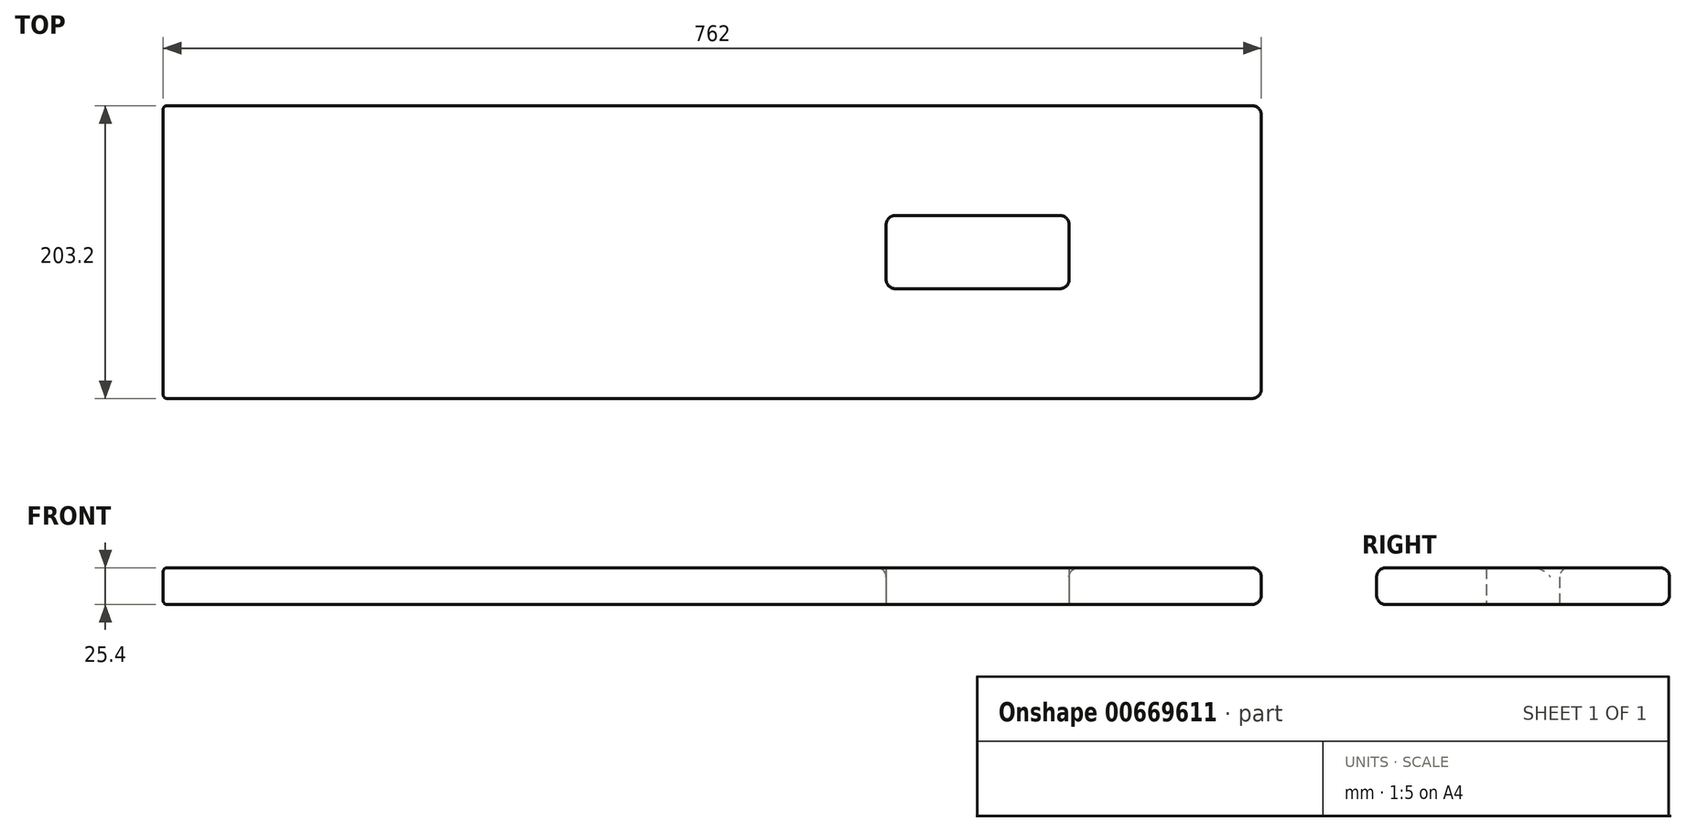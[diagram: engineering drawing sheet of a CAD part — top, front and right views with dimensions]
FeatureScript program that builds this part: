
annotation { "Feature Type Name" : "Feature", "Feature Type Description" : "" }
export const myFeature = defineFeature(function(context is Context, id is Id, definition is map)
    precondition{}
    {
        {
            var Q0;
            Q0=qCreatedBy(makeId("Front.planeOp"),FACE);
            var sketch = newSketch(context, id + "F0", { "sketchPlane" : qUnion([Q0])});
            skLineSegment(sketch, "E0.bottom", {"start": v(0, 0) * mm, "end": v(762, 0) * mm});
            skLineSegment(sketch, "E0.top", {"start": v(0, 25.4) * mm, "end": v(762, 25.4) * mm});
            skLineSegment(sketch, "E0.left", {"start": v(0, 0) * mm, "end": v(0, 25.4) * mm});
            skLineSegment(sketch, "E0.right", {"start": v(762, 0) * mm, "end": v(762, 25.4) * mm});
            skSolve(sketch);
        }
        {
            var Q0;
            Q0=makeQuery(id+"F0.imprint","IMPRINT",FACE,{"disambiguationData":[TD([[makeQuery(id+"F0.imprint","IMPRINT",EDGE,{"derivedFrom":sQuery(id+"F0.wireOp",EDGE,"E0.bottom")}),1.0]])]});
            extrude(context, id + "F1", {"entities" : qUnion([Q0]), "endBound" : BoundingType.SYMMETRIC, "depth" : 203.2 * mm, "offsetDistance" : 25.4 * mm});
        }
        {
            var Q0;
            Q0=makeQuery(id+"F1.opExtrude","CAP_EDGE",EDGE,{"disambiguationData":[OSD([sQuery(id+"F0.wireOp",EDGE,"E0.top")])],"isStart":false});
            var Q1;
            Q1=makeQuery(id+"F1.opExtrude","CAP_EDGE",EDGE,{"disambiguationData":[OSD([sQuery(id+"F0.wireOp",EDGE,"E0.bottom")])],"isStart":false});
            var Q2;
            Q2=makeQuery(id+"F1.opExtrude","CAP_EDGE",EDGE,{"disambiguationData":[OSD([sQuery(id+"F0.wireOp",EDGE,"E0.top")])],"isStart":true});
            var Q3;
            Q3=makeQuery(id+"F1.opExtrude","CAP_EDGE",EDGE,{"disambiguationData":[OSD([sQuery(id+"F0.wireOp",EDGE,"E0.bottom")])],"isStart":true});
            var Q4;
            Q4=makeQuery(id+"F1.opExtrude","SWEPT_EDGE",EDGE,{"disambiguationData":[OSD([sQuery(id+"F0.wireOp",EDGE,"E0.bottom"),sQuery(id+"F0.wireOp",EDGE,"E0.right")])]});
            var Q5;
            Q5=makeQuery(id+"F1.opExtrude","CAP_EDGE",EDGE,{"disambiguationData":[OSD([sQuery(id+"F0.wireOp",EDGE,"E0.right")])],"isStart":true});
            var Q6;
            Q6=makeQuery(id+"F1.opExtrude","CAP_EDGE",EDGE,{"disambiguationData":[OSD([sQuery(id+"F0.wireOp",EDGE,"E0.right")])],"isStart":false});
            fillet(context, id + "F2", {"entities" : qUnion([Q0, Q1, Q2, Q3, Q4, Q5, Q6]), "radius" : 6.35 * mm, "tangentPropagation" : true, "allowEdgeOverflow" : false});
        }
        {
            var Q0;
            Q0=makeQuery(id+"F1.opExtrude","SWEPT_EDGE",EDGE,{"disambiguationData":[OSD([sQuery(id+"F0.wireOp",EDGE,"E0.top"),sQuery(id+"F0.wireOp",EDGE,"E0.left")])]});
            var Q1;
            Q1=makeQuery(id+"F1.opExtrude","SWEPT_EDGE",EDGE,{"disambiguationData":[OSD([sQuery(id+"F0.wireOp",EDGE,"E0.bottom"),sQuery(id+"F0.wireOp",EDGE,"E0.left")])]});
            var Q2;
            Q2=makeQuery(id+"F2.opFillet","BLEND_EDGE",EDGE,{"blendedFrom":[makeQuery(id+"F1.opExtrude","CAP_EDGE",EDGE,{"disambiguationData":[OSD([sQuery(id+"F0.wireOp",EDGE,"E0.top")])],"isStart":false}),makeQuery(id+"F1.opExtrude","SWEPT_FACE",FACE,{"disambiguationData":[OSD([sQuery(id+"F0.wireOp",EDGE,"E0.left")])]})],"blendedInto":[makeQuery(id+"F1.opExtrude","SWEPT_FACE",FACE,{"disambiguationData":[OSD([sQuery(id+"F0.wireOp",EDGE,"E0.left")])]})]});
            fillet(context, id + "F3", {"entities" : qUnion([Q0, Q1, Q2]), "radius" : 2.54 * mm, "tangentPropagation" : true, "allowEdgeOverflow" : false});
        }
        {
            var Q0;
            Q0=makeQuery(id+"F1.opExtrude","SWEPT_EDGE",EDGE,{"disambiguationData":[OSD([sQuery(id+"F0.wireOp",EDGE,"E0.top"),sQuery(id+"F0.wireOp",EDGE,"E0.right")])]});
            fillet(context, id + "F4", {"entities" : qUnion([Q0]), "radius" : 6.35 * mm, "tangentPropagation" : true, "allowEdgeOverflow" : false});
        }
        {
            var Q0;
            Q0=makeQuery(id+"F1.opExtrude","SWEPT_FACE",FACE,{"disambiguationData":[OSD([sQuery(id+"F0.wireOp",EDGE,"E0.bottom")])]});
            var sketch = newSketch(context, id + "F5", { "sketchPlane" : qUnion([Q0])});
            skLineSegment(sketch, "E1", {"start": v(628.65, 0) * mm, "end": v(628.65, -25.4) * mm});
            skLineSegment(sketch, "E2", {"start": v(628.65, -25.4) * mm, "end": v(501.65, -25.4) * mm});
            skLineSegment(sketch, "E3", {"start": v(501.65, -25.4) * mm, "end": v(501.65, 0) * mm});
            skLineSegment(sketch, "E4", {"start": v(501.65, 0) * mm, "end": v(501.65, 25.4) * mm});
            skLineSegment(sketch, "E5", {"start": v(501.65, 25.4) * mm, "end": v(628.65, 25.4) * mm});
            skLineSegment(sketch, "E6", {"start": v(628.65, 25.4) * mm, "end": v(628.65, 0) * mm});
            skSolve(sketch);
        }
        {
            var Q0;
            Q0=makeQuery(id+"F5.imprint","IMPRINT",FACE,{"disambiguationData":[TD([[makeQuery(id+"F5.imprint","IMPRINT",EDGE,{"derivedFrom":sQuery(id+"F5.wireOp",EDGE,"E1")}),-1.0]])]});
            extrude(context, id + "F6", {"entities" : qUnion([Q0]), "operationType" : NewBodyOperationType.REMOVE, "endBound" : BoundingType.THROUGH_ALL, "oppositeDirection" : true, "depth" : 25.4 * mm, "offsetDistance" : 25.4 * mm});
        }
        {
            var Q0;
            Q0=makeQuery(id+"F6.boolean.opBoolean","COPY",EDGE,{"derivedFrom":makeQuery(id+"F6.opExtrude","CAP_EDGE",EDGE,{"disambiguationData":[OSD([sQuery(id+"F5.wireOp",EDGE,"E3"),sQuery(id+"F5.wireOp",EDGE,"E4")])],"isStart":true})});
            var Q1;
            Q1=makeQuery(id+"F6.boolean.opBoolean","COPY",EDGE,{"derivedFrom":makeQuery(id+"F6.opExtrude","SWEPT_EDGE",EDGE,{"disambiguationData":[OSD([sQuery(id+"F5.wireOp",EDGE,"E2"),sQuery(id+"F5.wireOp",EDGE,"E3")])]})});
            var Q2;
            Q2=makeQuery(id+"F6.boolean.opBoolean","COPY",EDGE,{"derivedFrom":makeQuery(id+"F6.opExtrude","SWEPT_EDGE",EDGE,{"disambiguationData":[OSD([sQuery(id+"F5.wireOp",EDGE,"E4"),sQuery(id+"F5.wireOp",EDGE,"E5")])]})});
            var Q3;
            Q3=makeQuery(id+"F6.boolean.opBoolean","COPY",EDGE,{"derivedFrom":makeQuery(id+"F6.opExtrude","SWEPT_EDGE",EDGE,{"disambiguationData":[OSD([sQuery(id+"F5.wireOp",EDGE,"E5"),sQuery(id+"F5.wireOp",EDGE,"E6")])]})});
            var Q4;
            Q4=makeQuery(id+"F6.boolean.opBoolean","COPY",EDGE,{"derivedFrom":makeQuery(id+"F6.opExtrude","SWEPT_EDGE",EDGE,{"disambiguationData":[OSD([sQuery(id+"F5.wireOp",EDGE,"E1"),sQuery(id+"F5.wireOp",EDGE,"E2")])]})});
            var Q5;
            Q5=makeQuery(id+"F6.boolean.opBoolean","INTERSECT",EDGE,{"derivedFrom":[makeQuery(id+"F1.opExtrude","SWEPT_FACE",FACE,{"disambiguationData":[OSD([sQuery(id+"F0.wireOp",EDGE,"E0.top")])]}),makeQuery(id+"F6.opExtrude","SWEPT_FACE",FACE,{"disambiguationData":[OSD([sQuery(id+"F5.wireOp",EDGE,"E2")])]})]});
            fillet(context, id + "F7", {"entities" : qUnion([Q0, Q1, Q2, Q3, Q4, Q5]), "radius" : 6.35 * mm, "tangentPropagation" : true, "allowEdgeOverflow" : false});
        }
    });
